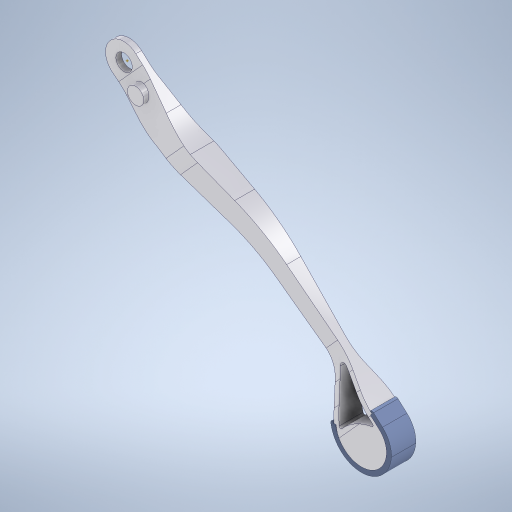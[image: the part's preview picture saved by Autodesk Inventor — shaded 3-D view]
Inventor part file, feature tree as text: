
AUTODESK INVENTOR PART (.ipt)
format: ipt  version: 2023 (Build 270158000, 158)  size: 949,248 bytes
history: native  units: mm
features: extrude x8, sketch x6, other x4, fillet x4, projected_geometry x1
ambient origin geometry x8: Origin, YZ Plane, XZ Plane, XY Plane, X Axis, Y Axis, Z Axis, Center Point
bodies: Body1 (feature_tree), Body2 (feature_tree)
feature tree (23):
  other  "솔리드1"
  extrude  "돌출1"  Depth=30.0mm TaperAngle=0.0deg
  other  "작업 평면1"
  extrude  "돌출2"  Depth=11.0mm
  other  "작업 평면2"
  sketch  "스케치3"
  fillet  "모깎기1"  Radius=33.0mm
  fillet  "모깎기2"  Radius=220.0mm
  fillet  "모깎기3"  Radius=11.5mm
  other  "작업 평면5"
  extrude  "돌출4"  Depth=130.0mm
  extrude  "돌출5"  Depth=48.5mm
  sketch  "스케치7"
  extrude  "돌출8"  Depth=11.0mm
  extrude  "돌출12"  Depth=220.0mm
  sketch  "스케치9"
  extrude  "돌출13"  Depth=11.5mm
  extrude  "돌출15"  TaperAngle=0.0deg  [1 undecoded]
  fillet  "모깎기4"  Radius=100.0mm
  sketch  "스케치1"
  sketch  "스케치2"
  sketch  "스케치5"
  projected_geometry  "투영된 루프1"
note: 1 required parameter value undecoded (feature->parameter linkage not recoverable at this tier; creation-order binding heuristic only, values carry confidence <= 0.55)
